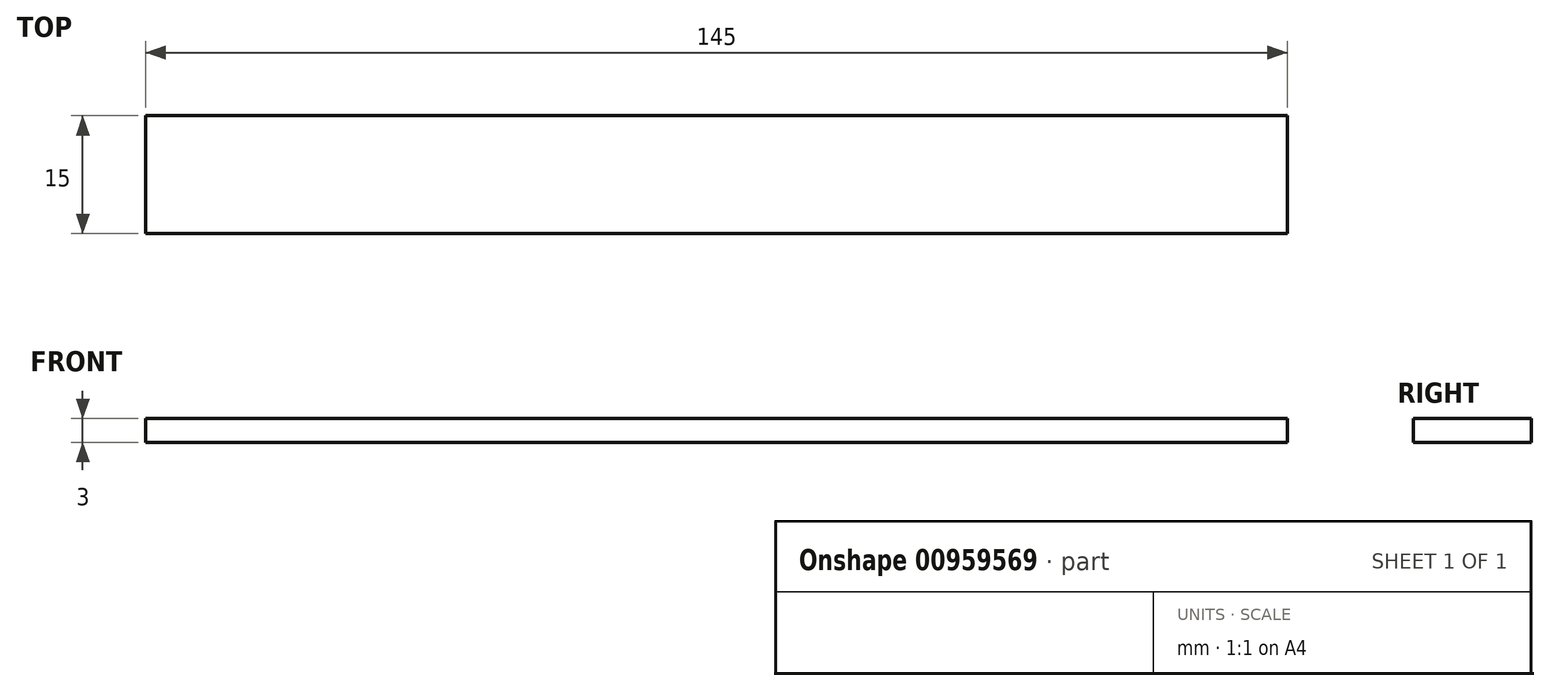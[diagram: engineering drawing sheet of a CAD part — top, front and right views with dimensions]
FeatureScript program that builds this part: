
annotation { "Feature Type Name" : "Feature", "Feature Type Description" : "" }
export const myFeature = defineFeature(function(context is Context, id is Id, definition is map)
    precondition{}
    {
        {
            var Q0;
            Q0=qCreatedBy(makeId("Top.planeOp"),FACE);
            var sketch = newSketch(context, id + "F0", { "sketchPlane" : qUnion([Q0])});
            skLineSegment(sketch, "E0.bottom", {"start": v(-70.32, -7.6) * mm, "end": v(74.68, -7.6) * mm});
            skLineSegment(sketch, "E0.top", {"start": v(-70.32, -22.6) * mm, "end": v(74.68, -22.6) * mm});
            skLineSegment(sketch, "E0.left", {"start": v(-70.32, -7.6) * mm, "end": v(-70.32, -22.6) * mm});
            skLineSegment(sketch, "E0.right", {"start": v(74.68, -7.6) * mm, "end": v(74.68, -22.6) * mm});
            skSolve(sketch);
        }
        {
            var Q0;
            Q0=makeQuery(id+"F0.imprint","IMPRINT",FACE,{"disambiguationData":[TD([[makeQuery(id+"F0.imprint","IMPRINT",EDGE,{"derivedFrom":sQuery(id+"F0.wireOp",EDGE,"E0.bottom")}),-1.0]])]});
            extrude(context, id + "F1", {"entities" : qUnion([Q0]), "depth" : 3 * mm, "offsetDistance" : 25 * mm});
        }
    });
